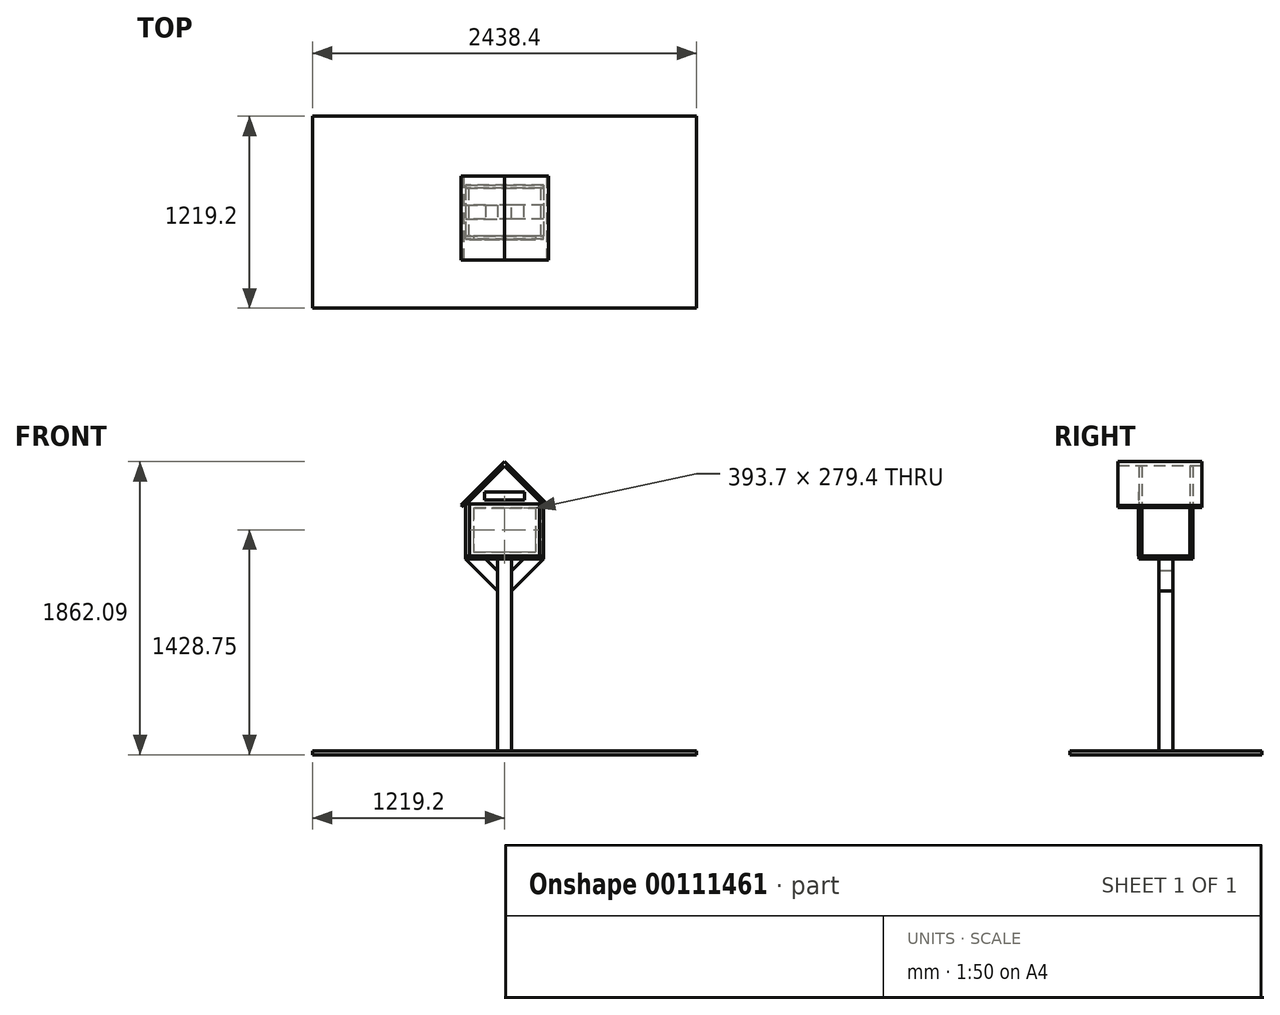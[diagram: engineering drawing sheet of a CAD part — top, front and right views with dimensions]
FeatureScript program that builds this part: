
annotation { "Feature Type Name" : "Feature", "Feature Type Description" : "" }
export const myFeature = defineFeature(function(context is Context, id is Id, definition is map)
    precondition{}
    {
        {
            var Q0;
            Q0=qCreatedBy(makeId("Top.planeOp"),FACE);
            var sketch = newSketch(context, id + "F0", { "sketchPlane" : qUnion([Q0])});
            skLineSegment(sketch, "E0.bottom", {"start": v(228.6, 152.4) * mm, "end": v(-228.6, 152.4) * mm});
            skLineSegment(sketch, "E0.top", {"start": v(228.6, -152.4) * mm, "end": v(-228.6, -152.4) * mm});
            skLineSegment(sketch, "E0.left", {"start": v(228.6, 152.4) * mm, "end": v(228.6, -152.4) * mm});
            skLineSegment(sketch, "E0.right", {"start": v(-228.6, 152.4) * mm, "end": v(-228.6, -152.4) * mm});
            skPoint(sketch, "E0.middle", {"position": v(0, 0) * mm});
            skSolve(sketch);
        }
        {
            var Q0;
            Q0=makeQuery(id+"F0.imprint","IMPRINT",FACE,{"disambiguationData":[TD([[makeQuery(id+"F0.imprint","IMPRINT",EDGE,{"derivedFrom":sQuery(id+"F0.wireOp",EDGE,"E0.bottom")}),1.0]])]});
            extrude(context, id + "F1", {"entities" : qUnion([Q0]), "depth" : 304.8 * mm});
        }
        {
            var Q0;
            Q0=makeQuery(id+"F1.opExtrude","CAP_FACE",FACE,{"disambiguationData":[OSD([sQuery(id+"F0.wireOp",EDGE,"E0.bottom"),sQuery(id+"F0.wireOp",EDGE,"E0.top"),sQuery(id+"F0.wireOp",EDGE,"E0.left"),sQuery(id+"F0.wireOp",EDGE,"E0.right")])],"isStart":true});
            var sketch = newSketch(context, id + "F2", { "sketchPlane" : qUnion([Q0])});
            skLineSegment(sketch, "E1.0", {"start": v(228.6, 152.4) * mm, "end": v(-228.6, 152.4) * mm});
            skLineSegment(sketch, "E1.1", {"start": v(-228.6, -152.4) * mm, "end": v(-228.6, 152.4) * mm});
            skLineSegment(sketch, "E2.0", {"start": v(228.6, -152.4) * mm, "end": v(-228.6, -152.4) * mm});
            skLineSegment(sketch, "E3.0", {"start": v(228.6, -152.4) * mm, "end": v(228.6, 152.4) * mm});
            skLineSegment(sketch, "E4.0", {"start": v(247.65, 171.45) * mm, "end": v(-247.65, 171.45) * mm});
            skLineSegment(sketch, "E4.1", {"start": v(247.65, -171.45) * mm, "end": v(247.65, 171.45) * mm});
            skLineSegment(sketch, "E4.2", {"start": v(247.65, -171.45) * mm, "end": v(-247.65, -171.45) * mm});
            skLineSegment(sketch, "E4.3", {"start": v(-247.65, -171.45) * mm, "end": v(-247.65, 171.45) * mm});
            skSolve(sketch);
        }
        {
            var Q0;
            Q0=makeQuery(id+"F2.imprint","IMPRINT",FACE,{"disambiguationData":[TD([[makeQuery(id+"F2.imprint","IMPRINT",EDGE,{"derivedFrom":sQuery(id+"F2.wireOp",EDGE,"E1.0")}),1.0]])]});
            var Q1;
            Q1=makeQuery(id+"F2.imprint","IMPRINT",FACE,{"disambiguationData":[TD([[makeQuery(id+"F2.imprint","IMPRINT",EDGE,{"derivedFrom":sQuery(id+"F2.wireOp",EDGE,"E1.0")}),-1.0]])]});
            extrude(context, id + "F3", {"entities" : qUnion([Q0, Q1]), "depth" : 19.05 * mm});
        }
        {
            var Q0;
            Q0=makeQuery(id+"F1.opExtrude","SWEPT_FACE",FACE,{"disambiguationData":[OSD([sQuery(id+"F0.wireOp",EDGE,"E0.top")])]});
            var sketch = newSketch(context, id + "F4", { "sketchPlane" : qUnion([Q0])});
            skLineSegment(sketch, "E5.0", {"start": v(-228.6, 304.8) * mm, "end": v(-228.6, 0) * mm});
            skLineSegment(sketch, "E6.0", {"start": v(228.6, 304.8) * mm, "end": v(-228.6, 304.8) * mm});
            skLineSegment(sketch, "E7.0", {"start": v(228.6, 304.8) * mm, "end": v(228.6, 0) * mm});
            skLineSegment(sketch, "E8.0", {"start": v(247.65, 323.85) * mm, "end": v(247.65, 0) * mm});
            skLineSegment(sketch, "E8.1", {"start": v(247.65, 323.85) * mm, "end": v(-247.65, 323.85) * mm});
            skLineSegment(sketch, "E8.2", {"start": v(-247.65, 323.85) * mm, "end": v(-247.65, 0) * mm});
            skLineSegment(sketch, "E9", {"start": v(-247.65, 0) * mm, "end": v(247.65, 0) * mm});
            skLineSegment(sketch, "E10", {"start": v(-247.65, 323.85) * mm, "end": v(0, 571.5) * mm});
            skLineSegment(sketch, "E11", {"start": v(0, 571.5) * mm, "end": v(247.65, 323.85) * mm});
            skSolve(sketch);
        }
        {
            var Q0;
            {var subQ0=sQuery(id+"F4.wireOp",EDGE,"E5.0");Q0=makeQuery(id+"F4.imprint","IMPRINT",FACE,{"disambiguationData":[TD([[makeQuery(id+"F4.imprint","IMPRINT",EDGE,{"derivedFrom":subQ0}),1.0]])]});}
            var Q1;
            {var subQ2=sQuery(id+"F4.wireOp",EDGE,"E5.0");Q1=makeQuery(id+"F4.imprint","IMPRINT",FACE,{"disambiguationData":[TD([[makeQuery(id+"F4.imprint","IMPRINT",EDGE,{"derivedFrom":subQ2}),-1.0]])]});}
            var Q2;
            Q2=makeQuery(id+"F4.imprint","IMPRINT",FACE,{"disambiguationData":[TD([[makeQuery(id+"F4.imprint","IMPRINT",EDGE,{"derivedFrom":sQuery(id+"F4.wireOp",EDGE,"E8.1")}),-1.0]])]});
            extrude(context, id + "F5", {"entities" : qUnion([Q0, Q1, Q2]), "depth" : 19.05 * mm});
        }
        {
            var Q0;
            Q0=makeQuery(id+"F5.opExtrude","SWEPT_BODY",BODY,{"disambiguationData":[OSD([sQuery(id+"F4.wireOp",EDGE,"E8.0"),sQuery(id+"F4.wireOp",EDGE,"E8.1"),sQuery(id+"F4.wireOp",EDGE,"E8.2"),sQuery(id+"F4.wireOp",EDGE,"E9")])]});
            transform(context, id + "F6", {"entities" : qUnion([Q0]), "transformType" : TransformType.TRANSLATION_3D, "dx" : 0 * mm, "dy" : 323.85 * mm, "dz" : 0 * mm, "makeCopy" : true});
        }
        {
            var Q0;
            Q0=makeQuery(id+"F1.opExtrude","SWEPT_FACE",FACE,{"disambiguationData":[OSD([sQuery(id+"F0.wireOp",EDGE,"E0.left")])]});
            var sketch = newSketch(context, id + "F7", { "sketchPlane" : qUnion([Q0])});
            skLineSegment(sketch, "E12.0.0", {"start": v(-152.4, 0) * mm, "end": v(152.4, 0) * mm});
            skLineSegment(sketch, "E12.0.1", {"start": v(152.4, 0) * mm, "end": v(152.4, 304.8) * mm});
            skLineSegment(sketch, "E12.0.2", {"start": v(152.4, 304.8) * mm, "end": v(-152.4, 304.8) * mm});
            skLineSegment(sketch, "E12.0.3", {"start": v(-152.4, 304.8) * mm, "end": v(-152.4, 0) * mm});
            skLineSegment(sketch, "E13.top", {"start": v(-152.4, 323.85) * mm, "end": v(152.4, 323.85) * mm});
            skLineSegment(sketch, "E13.left", {"start": v(-152.4, 0) * mm, "end": v(-152.4, 323.85) * mm});
            skLineSegment(sketch, "E13.right", {"start": v(152.4, 0) * mm, "end": v(152.4, 323.85) * mm});
            skSolve(sketch);
        }
        {
            var Q0;
            {var subQ0=sQuery(id+"F7.wireOp",EDGE,"E12.0.2");Q0=makeQuery(id+"F7.imprint","IMPRINT",FACE,{"disambiguationData":[TD([[makeQuery(id+"F7.imprint","IMPRINT",EDGE,{"derivedFrom":subQ0}),1.0]])]});}
            var Q1;
            {var subQ0=sQuery(id+"F7.wireOp",EDGE,"E12.0.2");Q1=makeQuery(id+"F7.imprint","IMPRINT",FACE,{"disambiguationData":[TD([[makeQuery(id+"F7.imprint","IMPRINT",EDGE,{"derivedFrom":subQ0}),-1.0]])]});}
            extrude(context, id + "F8", {"entities" : qUnion([Q0, Q1]), "depth" : 19.05 * mm});
        }
        {
            var Q0;
            Q0=makeQuery(id+"F8.opExtrude","SWEPT_BODY",BODY,{"disambiguationData":[OSD([sQuery(id+"F7.wireOp",EDGE,"E12.0.0"),sQuery(id+"F7.wireOp",EDGE,"E13.top"),sQuery(id+"F7.wireOp",EDGE,"E13.left"),sQuery(id+"F7.wireOp",EDGE,"E13.right")])]});
            transform(context, id + "F9", {"entities" : qUnion([Q0]), "transformType" : TransformType.TRANSLATION_3D, "dx" : -476.25 * mm, "dy" : 0 * mm, "dz" : 0 * mm, "makeCopy" : true});
        }
        {
            var Q0;
            Q0=makeQuery(id+"F6.opPattern","COPY",FACE,{"derivedFrom":makeQuery(id+"F5.opExtrude","CAP_FACE",FACE,{"disambiguationData":[OSD([sQuery(id+"F4.wireOp",EDGE,"E8.0"),sQuery(id+"F4.wireOp",EDGE,"E8.1"),sQuery(id+"F4.wireOp",EDGE,"E8.2"),sQuery(id+"F4.wireOp",EDGE,"E9")])],"isStart":false}),"instanceName":"1"});
            cPlane(context, id + "F10", {"entities" : qUnion([Q0]), "cplaneType" : CPlaneType.OFFSET, "offset" : 152.4 * mm, "width" : 152.4 * mm, "height" : 152.4 * mm});
        }
        {
            var Q0;
            Q0=qCreatedBy(id+"F10.planeOp",FACE);
            var sketch = newSketch(context, id + "F11", { "sketchPlane" : qUnion([Q0])});
            skLineSegment(sketch, "E14.0", {"start": v(-247.65, 323.85) * mm, "end": v(0, 571.5) * mm});
            skLineSegment(sketch, "E15.0", {"start": v(0, 571.5) * mm, "end": v(265.61, 305.89) * mm});
            skLineSegment(sketch, "E16.0", {"start": v(13.47, 584.97) * mm, "end": v(279.08, 319.36) * mm});
            skLineSegment(sketch, "E17.0", {"start": v(265.61, 305.89) * mm, "end": v(279.08, 319.36) * mm});
            skPoint(sketch, "E18.orphan", {"position": v(247.65, 323.85) * mm});
            skLineSegment(sketch, "E19", {"start": v(13.47, 584.97) * mm, "end": v(0, 571.5) * mm});
            skLineSegment(sketch, "E20.0", {"start": v(0, 598.44) * mm, "end": v(-13.47, 584.97) * mm});
            skLineSegment(sketch, "E20.1", {"start": v(-261.12, 337.32) * mm, "end": v(-13.47, 584.97) * mm});
            skLineSegment(sketch, "E21", {"start": v(0, 598.44) * mm, "end": v(13.47, 584.97) * mm});
            skLineSegment(sketch, "E22.0", {"start": v(-274.6, 323.85) * mm, "end": v(-261.12, 310.38) * mm});
            skLineSegment(sketch, "E23", {"start": v(-261.12, 337.32) * mm, "end": v(-274.6, 323.85) * mm});
            skLineSegment(sketch, "E24", {"start": v(-247.65, 323.85) * mm, "end": v(-261.12, 310.38) * mm});
            skSolve(sketch);
        }
        {
            var Q0;
            Q0=makeQuery(id+"F11.imprint","IMPRINT",FACE,{"disambiguationData":[TD([[makeQuery(id+"F11.imprint","IMPRINT",EDGE,{"derivedFrom":sQuery(id+"F11.wireOp",EDGE,"E14.0")}),1.0]])]});
            var Q1;
            Q1=makeQuery(id+"F11.imprint","IMPRINT",FACE,{"disambiguationData":[TD([[makeQuery(id+"F11.imprint","IMPRINT",EDGE,{"derivedFrom":sQuery(id+"F11.wireOp",EDGE,"E15.0")}),1.0]])]});
            extrude(context, id + "F12", {"entities" : qUnion([Q0, Q1]), "oppositeDirection" : true, "depth" : 228.6 * mm, "hasSecondDirection" : true, "secondDirectionOppositeDirection" : false, "secondDirectionDepth" : 304.8 * mm});
        }
        {
            var Q0;
            Q0=makeQuery(id+"F5.opExtrude","CAP_FACE",FACE,{"disambiguationData":[OSD([sQuery(id+"F4.wireOp",EDGE,"E8.0"),sQuery(id+"F4.wireOp",EDGE,"E8.2"),sQuery(id+"F4.wireOp",EDGE,"E9"),sQuery(id+"F4.wireOp",EDGE,"E10"),sQuery(id+"F4.wireOp",EDGE,"E11")])],"isStart":false});
            var sketch = newSketch(context, id + "F13", { "sketchPlane" : qUnion([Q0])});
            skLineSegment(sketch, "E25.0", {"start": v(247.65, 0) * mm, "end": v(196.85, 0) * mm, "construction": true});
            skLineSegment(sketch, "E26.0", {"start": v(-196.85, 304.8) * mm, "end": v(-196.85, 25.4) * mm});
            skLineSegment(sketch, "E27.0", {"start": v(196.85, 304.8) * mm, "end": v(196.85, 25.4) * mm});
            skLineSegment(sketch, "E28", {"start": v(-196.85, 304.8) * mm, "end": v(196.85, 304.8) * mm});
            skLineSegment(sketch, "E29", {"start": v(-196.85, 25.4) * mm, "end": v(196.85, 25.4) * mm});
            skLineSegment(sketch, "E30.trimOffspring", {"start": v(-196.85, 0) * mm, "end": v(-247.65, 0) * mm, "construction": true});
            skSolve(sketch);
        }
        {
            var Q0;
            Q0=makeQuery(id+"F13.imprint","IMPRINT",FACE,{"disambiguationData":[TD([[makeQuery(id+"F13.imprint","IMPRINT",EDGE,{"derivedFrom":sQuery(id+"F13.wireOp",EDGE,"E26.0")}),1.0]])]});
            extrude(context, id + "F14", {"entities" : qUnion([Q0]), "operationType" : NewBodyOperationType.REMOVE, "endBound" : BoundingType.UP_TO_NEXT, "oppositeDirection" : true, "depth" : 25.4 * mm});
        }
        {
            var Q0;
            Q0=makeQuery(id+"F5.opExtrude","CAP_FACE",FACE,{"disambiguationData":[OSD([sQuery(id+"F4.wireOp",EDGE,"E8.0"),sQuery(id+"F4.wireOp",EDGE,"E8.2"),sQuery(id+"F4.wireOp",EDGE,"E9"),sQuery(id+"F4.wireOp",EDGE,"E10"),sQuery(id+"F4.wireOp",EDGE,"E11")])],"isStart":false});
            var sketch = newSketch(context, id + "F15", { "sketchPlane" : qUnion([Q0])});
            skLineSegment(sketch, "E31.0", {"start": v(-222.25, 330.2) * mm, "end": v(-222.25, 0) * mm});
            skLineSegment(sketch, "E31.1", {"start": v(-222.25, 330.2) * mm, "end": v(222.25, 330.2) * mm});
            skLineSegment(sketch, "E31.2", {"start": v(222.25, 330.2) * mm, "end": v(222.25, 0) * mm});
            skLineSegment(sketch, "E31.3", {"start": v(-222.25, 0) * mm, "end": v(222.25, 0) * mm});
            skSolve(sketch);
        }
        {
            var Q0;
            Q0 = qSketchRegion(id + "F15", true);
            extrude(context, id + "F16", {"entities" : qUnion([Q0]), "depth" : 3.17 * mm});
        }
        {
            var Q0;
            Q0=makeQuery(id+"F3.opExtrude","CAP_FACE",FACE,{"disambiguationData":[OSD([sQuery(id+"F2.wireOp",EDGE,"E4.0"),sQuery(id+"F2.wireOp",EDGE,"E4.1"),sQuery(id+"F2.wireOp",EDGE,"E4.2"),sQuery(id+"F2.wireOp",EDGE,"E4.3")])],"isStart":false});
            var sketch = newSketch(context, id + "F17", { "sketchPlane" : qUnion([Q0])});
            skLineSegment(sketch, "E32", {"start": v(-247.65, 171.45) * mm, "end": v(247.65, -171.45) * mm, "construction": true});
            skLineSegment(sketch, "E33.bottom", {"start": v(44.45, 44.45) * mm, "end": v(-44.45, 44.45) * mm});
            skLineSegment(sketch, "E33.top", {"start": v(44.45, -44.45) * mm, "end": v(-44.45, -44.45) * mm});
            skLineSegment(sketch, "E33.left", {"start": v(44.45, 44.45) * mm, "end": v(44.45, -44.45) * mm});
            skLineSegment(sketch, "E33.right", {"start": v(-44.45, 44.45) * mm, "end": v(-44.45, -44.45) * mm});
            skPoint(sketch, "E33.middle", {"position": v(0, 0) * mm});
            skSolve(sketch);
        }
        {
            var Q0;
            Q0=makeQuery(id+"F17.imprint","IMPRINT",FACE,{"disambiguationData":[TD([[makeQuery(id+"F17.imprint","IMPRINT",EDGE,{"derivedFrom":sQuery(id+"F17.wireOp",EDGE,"E33.bottom")}),1.0]])]});
            extrude(context, id + "F18", {"entities" : qUnion([Q0]), "depth" : 1219.2 * mm});
        }
        {
            var Q0;
            Q0=makeQuery(id+"F18.opExtrude","SWEPT_FACE",FACE,{"disambiguationData":[OSD([sQuery(id+"F17.wireOp",EDGE,"E33.bottom")])]});
            var sketch = newSketch(context, id + "F19", { "sketchPlane" : qUnion([Q0])});
            skLineSegment(sketch, "E34.0", {"start": v(-44.45, -1238.25) * mm, "end": v(-44.45, -19.05) * mm});
            skLineSegment(sketch, "E35.0", {"start": v(44.45, -1238.25) * mm, "end": v(44.45, -19.05) * mm});
            skLineSegment(sketch, "E36.0.1", {"start": v(247.65, -19.05) * mm, "end": v(-247.65, -19.05) * mm});
            skLineSegment(sketch, "E36.0.3", {"start": v(-247.65, -19.05) * mm, "end": v(247.65, -19.05) * mm});
            skLineSegment(sketch, "E37", {"start": v(247.65, -19.05) * mm, "end": v(44.45, -222.25) * mm});
            skLineSegment(sketch, "E38.0", {"start": v(121.93, -19.05) * mm, "end": v(44.45, -96.53) * mm});
            skLineSegment(sketch, "E39", {"start": v(0, -19.05) * mm, "end": v(0, -360.1) * mm, "construction": true});
            skLineSegment(sketch, "E40.MirrorCS", {"start": v(-247.65, -19.05) * mm, "end": v(-44.45, -222.25) * mm});
            skLineSegment(sketch, "E41.MirrorCS", {"start": v(-121.93, -19.05) * mm, "end": v(-44.45, -96.53) * mm});
            skSolve(sketch);
        }
        {
            var Q0;
            {var subQ0=sQuery(id+"F19.wireOp",EDGE,"E40.MirrorCS");Q0=makeQuery(id+"F19.imprint","IMPRINT",FACE,{"disambiguationData":[TD([[makeQuery(id+"F19.imprint","IMPRINT",EDGE,{"derivedFrom":subQ0}),1.0]])]});}
            var Q1;
            {var subQ0=sQuery(id+"F19.wireOp",EDGE,"E37");Q1=makeQuery(id+"F19.imprint","IMPRINT",FACE,{"disambiguationData":[TD([[makeQuery(id+"F19.imprint","IMPRINT",EDGE,{"derivedFrom":subQ0}),-1.0]])]});}
            var Q2;
            Q2=makeQuery(id+"F18.opExtrude","SWEPT_FACE",FACE,{"disambiguationData":[OSD([sQuery(id+"F17.wireOp",EDGE,"E33.top")])]});
            extrude(context, id + "F20", {"entities" : qUnion([Q0, Q1]), "endBound" : BoundingType.UP_TO_SURFACE, "oppositeDirection" : true, "endBoundEntityFace" : qUnion([Q2]), "depth" : 25.4 * mm});
        }
        {
            var Q0;
            Q0=makeQuery(id+"F5.opExtrude","CAP_FACE",FACE,{"disambiguationData":[OSD([sQuery(id+"F4.wireOp",EDGE,"E8.0"),sQuery(id+"F4.wireOp",EDGE,"E8.2"),sQuery(id+"F4.wireOp",EDGE,"E9"),sQuery(id+"F4.wireOp",EDGE,"E10"),sQuery(id+"F4.wireOp",EDGE,"E11")])],"isStart":false});
            var sketch = newSketch(context, id + "F21", { "sketchPlane" : qUnion([Q0])});
            skLineSegment(sketch, "E42.bottom", {"start": v(-127, 406.4) * mm, "end": v(127, 406.4) * mm});
            skLineSegment(sketch, "E42.top", {"start": v(-127, 355.6) * mm, "end": v(127, 355.6) * mm});
            skLineSegment(sketch, "E42.left", {"start": v(-127, 406.4) * mm, "end": v(-127, 355.6) * mm});
            skLineSegment(sketch, "E42.right", {"start": v(127, 406.4) * mm, "end": v(127, 355.6) * mm});
            skSolve(sketch);
        }
        {
            var Q0;
            Q0=makeQuery(id+"F21.imprint","IMPRINT",FACE,{"disambiguationData":[TD([[makeQuery(id+"F21.imprint","IMPRINT",EDGE,{"derivedFrom":sQuery(id+"F21.wireOp",EDGE,"E42.bottom")}),-1.0]])]});
            extrude(context, id + "F22", {"entities" : qUnion([Q0]), "depth" : 3.17 * mm});
        }
        {
            var Q0;
            Q0=makeQuery(id+"F18.opExtrude","CAP_FACE",FACE,{"disambiguationData":[OSD([sQuery(id+"F17.wireOp",EDGE,"E33.bottom"),sQuery(id+"F17.wireOp",EDGE,"E33.top"),sQuery(id+"F17.wireOp",EDGE,"E33.left"),sQuery(id+"F17.wireOp",EDGE,"E33.right")])],"isStart":false});
            var sketch = newSketch(context, id + "F23", { "sketchPlane" : qUnion([Q0])});
            skLineSegment(sketch, "E43", {"start": v(-44.45, 44.45) * mm, "end": v(44.45, -44.45) * mm, "construction": true});
            skLineSegment(sketch, "E44.bottom", {"start": v(1219.2, 609.6) * mm, "end": v(-1219.2, 609.6) * mm});
            skLineSegment(sketch, "E44.top", {"start": v(1219.2, -609.6) * mm, "end": v(-1219.2, -609.6) * mm});
            skLineSegment(sketch, "E44.left", {"start": v(1219.2, 609.6) * mm, "end": v(1219.2, -609.6) * mm});
            skLineSegment(sketch, "E44.right", {"start": v(-1219.2, 609.6) * mm, "end": v(-1219.2, -609.6) * mm});
            skPoint(sketch, "E44.middle", {"position": v(0, 0) * mm});
            skSolve(sketch);
        }
        {
            var Q0;
            Q0 = qSketchRegion(id + "F23", true);
            extrude(context, id + "F24", {"entities" : qUnion([Q0]), "depth" : 25.4 * mm});
        }
    });
